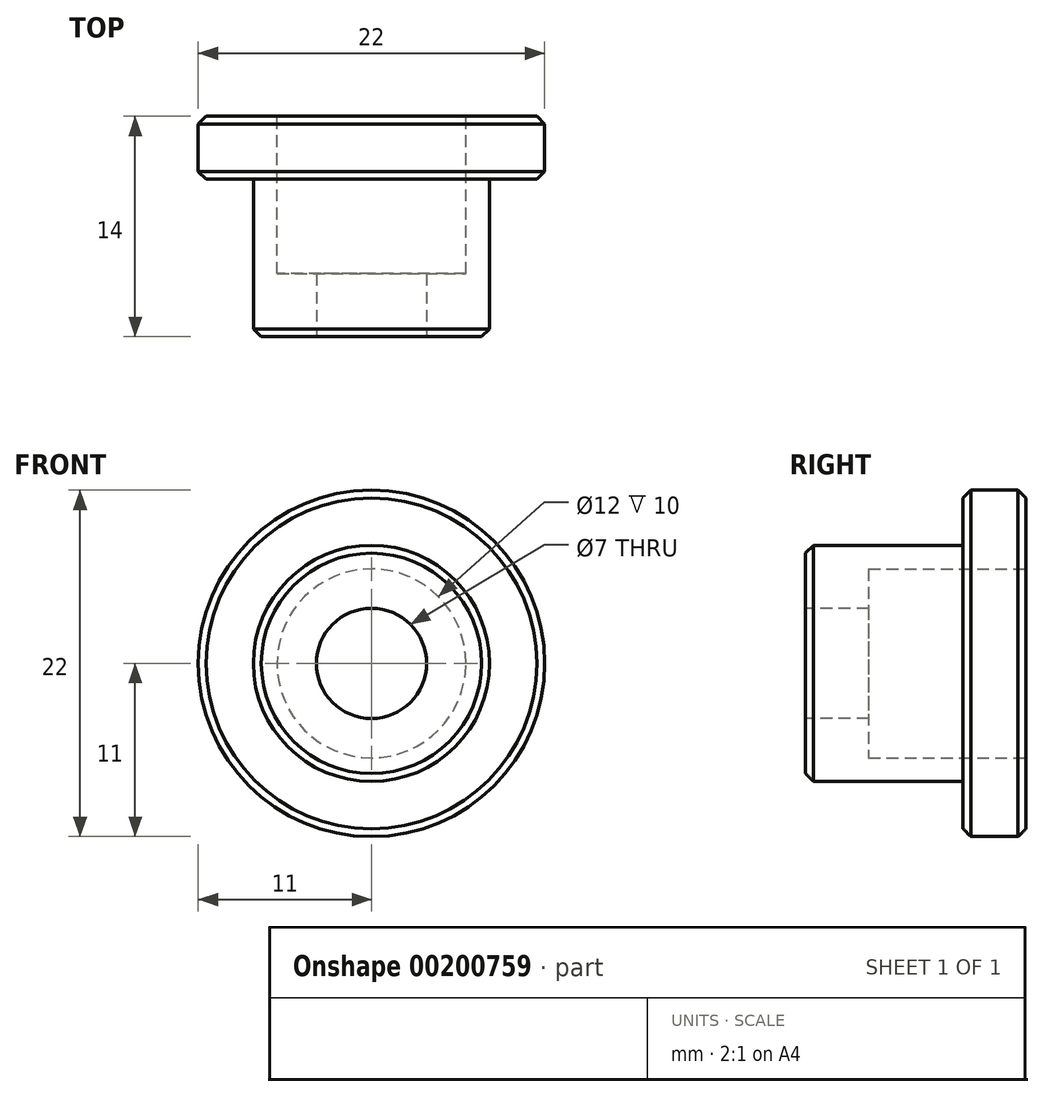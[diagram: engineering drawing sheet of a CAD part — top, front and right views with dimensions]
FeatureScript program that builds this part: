
annotation { "Feature Type Name" : "Feature", "Feature Type Description" : "" }
export const myFeature = defineFeature(function(context is Context, id is Id, definition is map)
    precondition{}
    {
        {
            var Q0;
            Q0=qCreatedBy(makeId("Front.planeOp"),FACE);
            var sketch = newSketch(context, id + "F0", { "sketchPlane" : qUnion([Q0])});
            skCircle(sketch, "E0", {"center": v(0, 0) * mm, "radius": 11 * mm});
            skSolve(sketch);
        }
        {
            var Q0;
            Q0=qSketchRegion(id+"F0",true);
            extrude(context, id + "F1", {"entities" : qUnion([Q0]), "depth" : 4 * mm});
        }
        {
            var Q0;
            Q0=makeQuery(id+"F1.opExtrude","CAP_FACE",FACE,{"disambiguationData":[OSD([sQuery(id+"F0.wireOp",EDGE,"E0")])],"isStart":false});
            var sketch = newSketch(context, id + "F2", { "sketchPlane" : qUnion([Q0])});
            skCircle(sketch, "E1", {"center": v(0, 0) * mm, "radius": 7.5 * mm});
            skSolve(sketch);
        }
        {
            var Q0;
            Q0=qSketchRegion(id+"F2",true);
            extrude(context, id + "F5", {"entities" : qUnion([Q0]), "operationType" : NewBodyOperationType.ADD, "depth" : 10 * mm});
        }
        {
            var Q0;
            Q0=makeQuery(id+"F1.opExtrude","CAP_FACE",FACE,{"disambiguationData":[OSD([sQuery(id+"F0.wireOp",EDGE,"E0")])],"isStart":true});
            var sketch = newSketch(context, id + "F3", { "sketchPlane" : qUnion([Q0])});
            skCircle(sketch, "E2", {"center": v(0, 0) * mm, "radius": 6 * mm});
            skSolve(sketch);
        }
        {
            var Q0;
            Q0=qSketchRegion(id+"F3",true);
            extrude(context, id + "F6", {"entities" : qUnion([Q0]), "operationType" : NewBodyOperationType.REMOVE, "oppositeDirection" : true, "depth" : 10 * mm});
        }
        {
            var Q0;
            Q0=makeQuery(id+"F5.opExtrude","CAP_FACE",FACE,{"disambiguationData":[OSD([sQuery(id+"F2.wireOp",EDGE,"E1")])],"isStart":false});
            var sketch = newSketch(context, id + "F7", { "sketchPlane" : qUnion([Q0])});
            skCircle(sketch, "E3", {"center": v(0, 0) * mm, "radius": 3.5 * mm});
            skSolve(sketch);
        }
        {
            var Q0;
            Q0=qSketchRegion(id+"F7",true);
            extrude(context, id + "F4", {"entities" : qUnion([Q0]), "operationType" : NewBodyOperationType.REMOVE, "oppositeDirection" : true, "depth" : 25 * mm});
        }
        {
            var Q0;
            Q0=makeQuery(id+"F5.opExtrude","CAP_EDGE",EDGE,{"disambiguationData":[OSD([sQuery(id+"F2.wireOp",EDGE,"E1")])],"isStart":false});
            var Q1;
            Q1=makeQuery(id+"F4.boolean.opBoolean","COPY",EDGE,{"derivedFrom":makeQuery(id+"F4.opExtrude","CAP_EDGE",EDGE,{"disambiguationData":[OSD([sQuery(id+"F7.wireOp",EDGE,"E3")])],"isStart":true})});
            var Q2;
            Q2=makeQuery(id+"F1.opExtrude","SWEPT_FACE",FACE,{"disambiguationData":[OSD([sQuery(id+"F0.wireOp",EDGE,"E0")])]});
            chamfer(context, id + "F8", {"entities" : qUnion([Q0, Q1, Q2]), "width" : 0.5 * mm, "tangentPropagation" : true});
        }
    });
